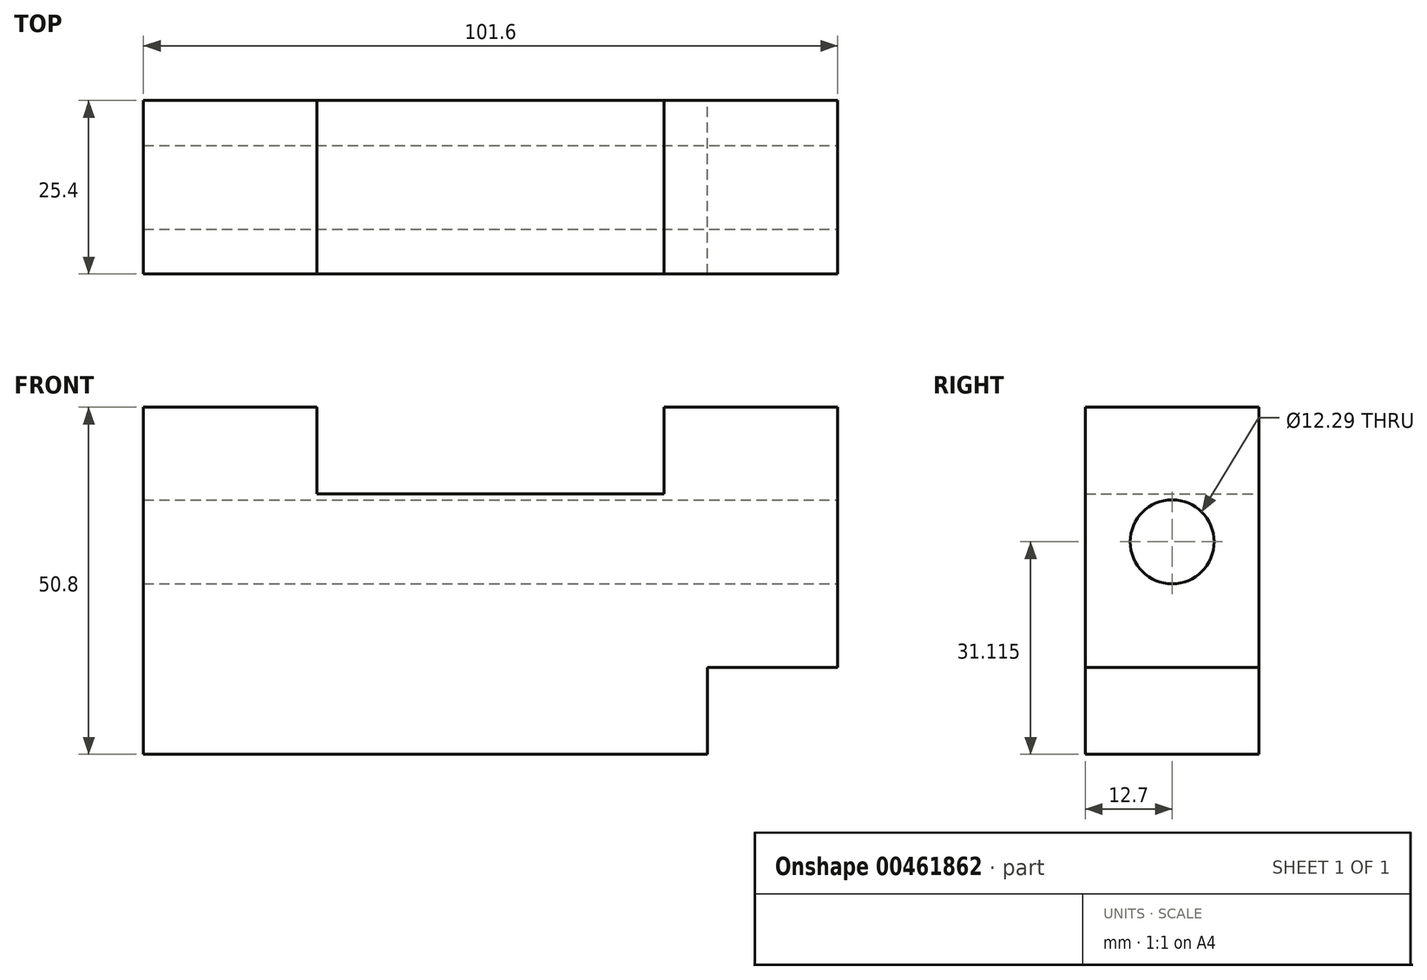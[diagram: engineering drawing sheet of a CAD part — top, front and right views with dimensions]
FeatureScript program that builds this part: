
annotation { "Feature Type Name" : "Feature", "Feature Type Description" : "" }
export const myFeature = defineFeature(function(context is Context, id is Id, definition is map)
    precondition{}
    {
        {
            var Q0;
            Q0=qCreatedBy(makeId("Front.planeOp"),FACE);
            var sketch = newSketch(context, id + "F0", { "sketchPlane" : qUnion([Q0])});
            skLineSegment(sketch, "E0.bottom", {"start": v(50.8, 25.4) * mm, "end": v(-50.8, 25.4) * mm});
            skLineSegment(sketch, "E0.top", {"start": v(50.8, -25.4) * mm, "end": v(-50.8, -25.4) * mm});
            skLineSegment(sketch, "E0.left", {"start": v(50.8, 25.4) * mm, "end": v(50.8, -25.4) * mm});
            skLineSegment(sketch, "E0.right", {"start": v(-50.8, 25.4) * mm, "end": v(-50.8, -25.4) * mm});
            skPoint(sketch, "E0.middle", {"position": v(0, 0) * mm});
            skSolve(sketch);
        }
        {
            var Q0;
            Q0=makeQuery(id+"F0.imprint","IMPRINT",FACE,{"disambiguationData":[TD([[makeQuery(id+"F0.imprint","IMPRINT",EDGE,{"derivedFrom":sQuery(id+"F0.wireOp",EDGE,"E0.bottom")}),1.0]])]});
            extrude(context, id + "F1", {"entities" : qUnion([Q0]), "depth" : 25.4 * mm});
        }
        {
            var Q0;
            Q0=qCreatedBy(makeId("Front.planeOp"),FACE);
            var sketch = newSketch(context, id + "F2", { "sketchPlane" : qUnion([Q0])});
            skLineSegment(sketch, "E1.bottom", {"start": v(25.4, 25.4) * mm, "end": v(-25.4, 25.4) * mm});
            skLineSegment(sketch, "E1.top", {"start": v(25.4, 12.7) * mm, "end": v(-25.4, 12.7) * mm});
            skLineSegment(sketch, "E1.left", {"start": v(25.4, 25.4) * mm, "end": v(25.4, 12.7) * mm});
            skLineSegment(sketch, "E1.right", {"start": v(-25.4, 25.4) * mm, "end": v(-25.4, 12.7) * mm});
            skSolve(sketch);
        }
        {
            var Q0;
            Q0 = qSketchRegion(id + "F2", true);
            extrude(context, id + "F3", {"entities" : qUnion([Q0]), "operationType" : NewBodyOperationType.REMOVE, "endBound" : BoundingType.THROUGH_ALL, "depth" : 25.4 * mm});
        }
        {
            var Q0;
            Q0=qCreatedBy(makeId("Front.planeOp"),FACE);
            var sketch = newSketch(context, id + "F4", { "sketchPlane" : qUnion([Q0])});
            skLineSegment(sketch, "E2.bottom", {"start": v(50.8, -25.4) * mm, "end": v(31.75, -25.4) * mm});
            skLineSegment(sketch, "E2.top", {"start": v(50.8, -12.7) * mm, "end": v(31.75, -12.7) * mm});
            skLineSegment(sketch, "E2.left", {"start": v(50.8, -25.4) * mm, "end": v(50.8, -12.7) * mm});
            skLineSegment(sketch, "E2.right", {"start": v(31.75, -25.4) * mm, "end": v(31.75, -12.7) * mm});
            skSolve(sketch);
        }
        {
            var Q0;
            Q0 = qSketchRegion(id + "F4", true);
            extrude(context, id + "F5", {"entities" : qUnion([Q0]), "operationType" : NewBodyOperationType.REMOVE, "endBound" : BoundingType.THROUGH_ALL, "depth" : 25.4 * mm});
        }
        {
            var Q0;
            Q0=qCreatedBy(makeId("Right.planeOp"),FACE);
            var sketch = newSketch(context, id + "F6", { "sketchPlane" : qUnion([Q0])});
            skCircle(sketch, "E3", {"center": v(-12.7, 5.72) * mm, "radius": 6.15 * mm});
            skSolve(sketch);
        }
        {
            var Q0;
            Q0 = qSketchRegion(id + "F6", true);
            extrude(context, id + "F7", {"entities" : qUnion([Q0]), "operationType" : NewBodyOperationType.REMOVE, "oppositeDirection" : true, "depth" : 50.8 * mm});
        }
        {
            var Q0;
            Q0 = qSketchRegion(id + "F6", true);
            extrude(context, id + "F8", {"entities" : qUnion([Q0]), "operationType" : NewBodyOperationType.REMOVE, "endBound" : BoundingType.THROUGH_ALL, "depth" : 50.8 * mm});
        }
    });
